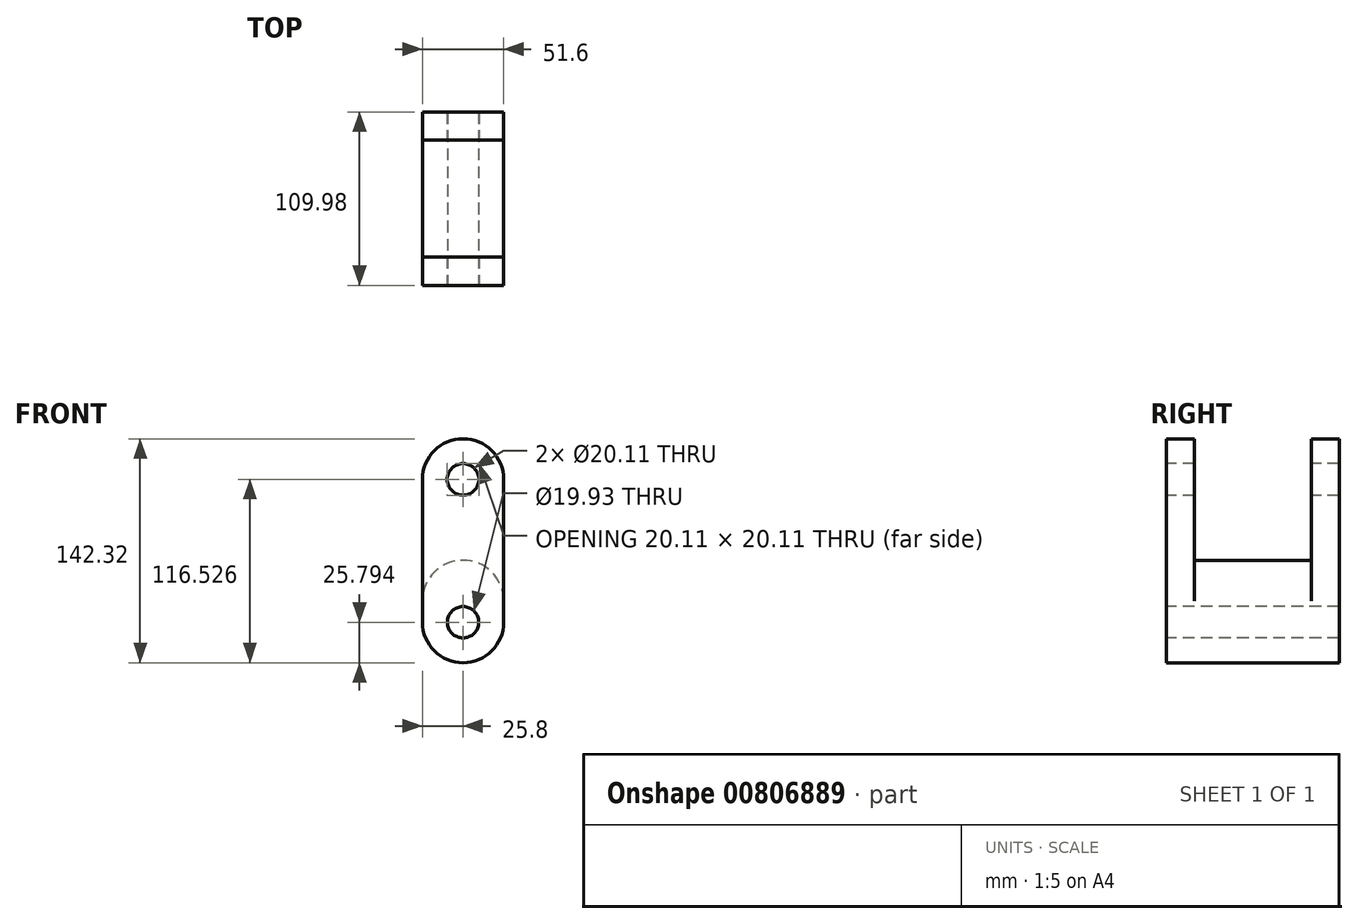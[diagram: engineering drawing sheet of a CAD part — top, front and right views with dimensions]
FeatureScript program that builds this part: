
annotation { "Feature Type Name" : "Feature", "Feature Type Description" : "" }
export const myFeature = defineFeature(function(context is Context, id is Id, definition is map)
    precondition{}
    {
        {
            var Q0;
            Q0=qCreatedBy(makeId("Front.planeOp"),FACE);
            var sketch = newSketch(context, id + "F0", { "sketchPlane" : qUnion([Q0])});
            skLineSegment(sketch, "E0.left", {"start": v(25.8, -45.37) * mm, "end": v(25.8, 45.37) * mm});
            skLineSegment(sketch, "E0.right", {"start": v(-25.8, -45.37) * mm, "end": v(-25.8, 45.37) * mm});
            skPoint(sketch, "E0.middle", {"position": v(0, 0) * mm});
            skArc(sketch, "E1", {"start": v(25.8, 45.37) * mm, "mid": v(0, 71.16) * mm, "end": v(-25.8, 45.37) * mm});
            skArc(sketch, "E2", {"start": v(-25.8, -45.37) * mm, "mid": v(0, -71.16) * mm, "end": v(25.8, -45.37) * mm});
            skCircle(sketch, "E3", {"center": v(0, -45.37) * mm, "radius": 9.96 * mm});
            skCircle(sketch, "E4", {"center": v(0, 45.37) * mm, "radius": 10.06 * mm});
            skSolve(sketch);
        }
        {
            var Q0;
            Q0=makeQuery(id+"F0.imprint","IMPRINT",FACE,{"disambiguationData":[TD([[makeQuery(id+"F0.imprint","IMPRINT",EDGE,{"derivedFrom":sQuery(id+"F0.wireOp",EDGE,"E0.left")}),1.0]])]});
            extrude(context, id + "F1", {"entities" : qUnion([Q0]), "oppositeDirection" : true, "depth" : 109.98 * mm, "offsetDistance" : 25.4 * mm});
        }
        {
            var Q0;
            Q0=makeQuery(id+"F1.opExtrude","SWEPT_FACE",FACE,{"disambiguationData":[OSD([sQuery(id+"F0.wireOp",EDGE,"E0.left")])]});
            var sketch = newSketch(context, id + "F2", { "sketchPlane" : qUnion([Q0])});
            skLineSegment(sketch, "E5.bottom", {"start": v(18.03, -31.76) * mm, "end": v(92.28, -31.76) * mm});
            skLineSegment(sketch, "E5.top", {"start": v(18.03, 78.47) * mm, "end": v(92.28, 78.47) * mm});
            skLineSegment(sketch, "E5.left", {"start": v(18.03, -31.76) * mm, "end": v(18.03, 78.47) * mm});
            skLineSegment(sketch, "E5.right", {"start": v(92.28, -31.76) * mm, "end": v(92.28, 78.47) * mm});
            skSolve(sketch);
        }
        {
            var Q0;
            Q0 = qSketchRegion(id + "F2", true);
            extrude(context, id + "F3", {"entities" : qUnion([Q0]), "operationType" : NewBodyOperationType.REMOVE, "endBound" : BoundingType.THROUGH_ALL, "oppositeDirection" : true, "depth" : 25.4 * mm, "offsetDistance" : 25.4 * mm});
        }
        {
            var Q0;
            Q0=makeQuery(id+"F3.boolean.opBoolean","COPY",FACE,{"derivedFrom":makeQuery(id+"F3.opExtrude","SWEPT_FACE",FACE,{"disambiguationData":[OSD([sQuery(id+"F2.wireOp",EDGE,"E5.right")])]})});
            var sketch = newSketch(context, id + "F4", { "sketchPlane" : qUnion([Q0])});
            skArc(sketch, "E6", {"start": v(25.8, -31.76) * mm, "mid": v(0, -5.96) * mm, "end": v(-25.8, -31.76) * mm});
            skSolve(sketch);
        }
        {
            var Q0;
            Q0=makeQuery(id+"F4.imprint","IMPRINT",FACE,{"disambiguationData":[TD([[makeQuery(id+"F4.imprint","IMPRINT",EDGE,{"derivedFrom":sQuery(id+"F4.wireOp",EDGE,"E6")}),1.0]])]});
            extrude(context, id + "F5", {"entities" : qUnion([Q0]), "operationType" : NewBodyOperationType.ADD, "depth" : 79.5 * mm, "offsetDistance" : 25.4 * mm});
        }
    });
